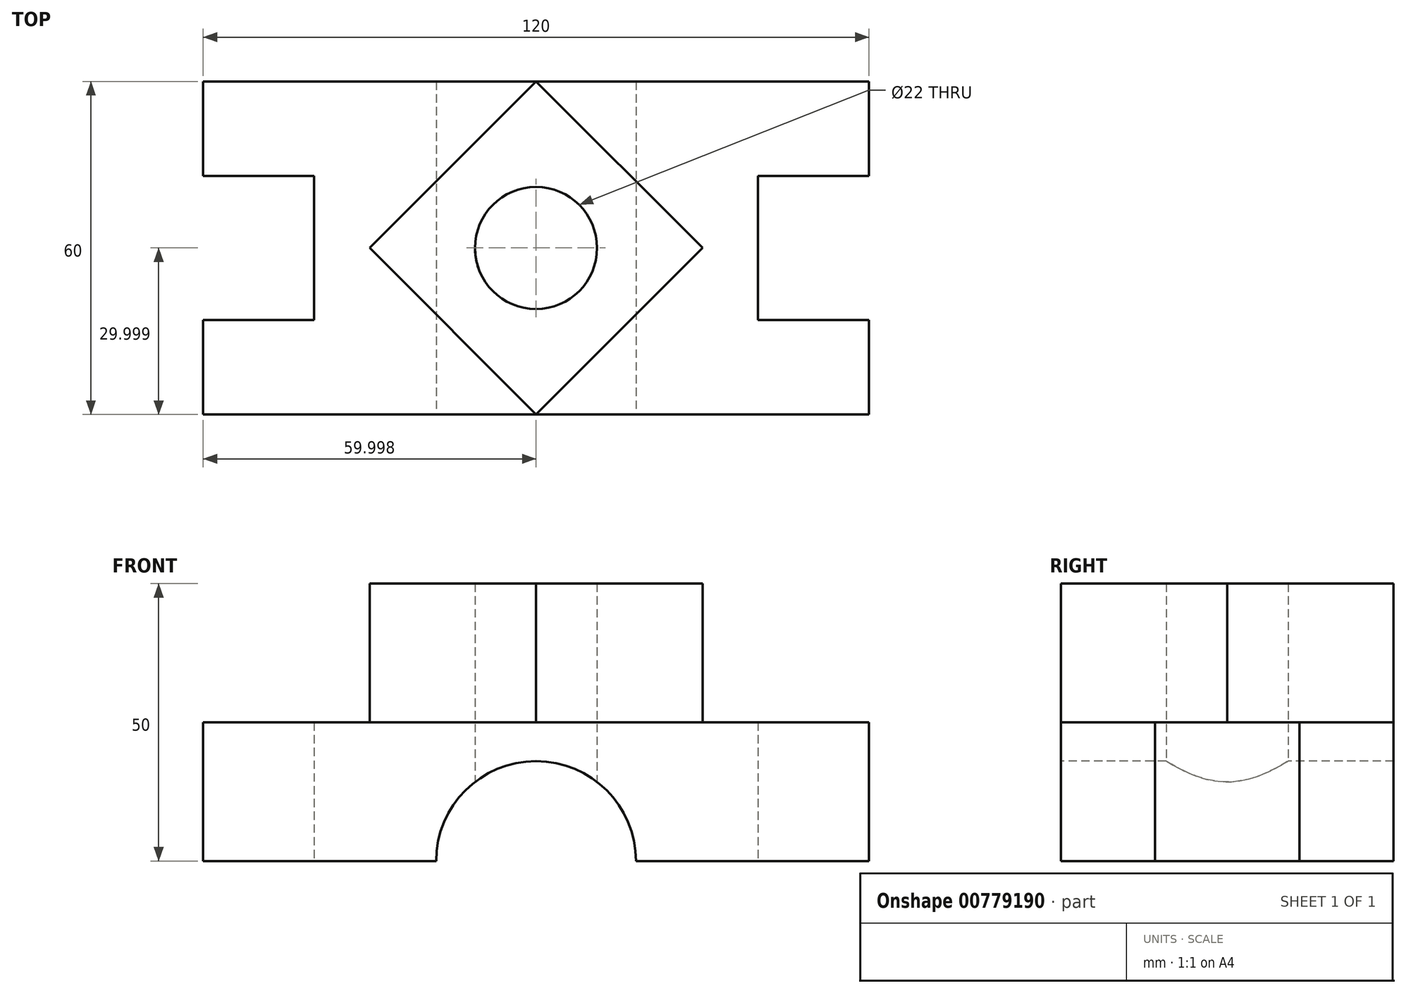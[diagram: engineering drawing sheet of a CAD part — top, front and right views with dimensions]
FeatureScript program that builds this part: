
annotation { "Feature Type Name" : "Feature", "Feature Type Description" : "" }
export const myFeature = defineFeature(function(context is Context, id is Id, definition is map)
    precondition{}
    {
        {
            var Q0;
            Q0=qCreatedBy(makeId("Top.planeOp"),FACE);
            var sketch = newSketch(context, id + "F0", { "sketchPlane" : qUnion([Q0])});
            skLineSegment(sketch, "E0.bottom", {"start": v(-146.92, 73.64) * mm, "end": v(-26.92, 73.64) * mm});
            skLineSegment(sketch, "E0.top", {"start": v(-146.92, 13.64) * mm, "end": v(-26.92, 13.64) * mm});
            skLineSegment(sketch, "E0.left", {"start": v(-146.92, 73.64) * mm, "end": v(-146.92, 56.64) * mm});
            skLineSegment(sketch, "E0.right", {"start": v(-26.92, 73.64) * mm, "end": v(-26.92, 56.64) * mm});
            skLineSegment(sketch, "E1", {"start": v(-146.92, 73.64) * mm, "end": v(-86.92, 73.64) * mm});
            skLineSegment(sketch, "E2", {"start": v(-86.92, 73.64) * mm, "end": v(-86.92, 43.64) * mm});
            skLineSegment(sketch, "E3", {"start": v(-86.92, 43.64) * mm, "end": v(-46.92, 43.64) * mm});
            skLineSegment(sketch, "E4", {"start": v(-26.92, 30.64) * mm, "end": v(-46.92, 30.64) * mm});
            skLineSegment(sketch, "E5", {"start": v(-46.92, 30.64) * mm, "end": v(-46.92, 56.64) * mm});
            skLineSegment(sketch, "E6", {"start": v(-46.92, 56.64) * mm, "end": v(-26.92, 56.64) * mm});
            skLineSegment(sketch, "E7.trimOffspring", {"start": v(-26.92, 30.64) * mm, "end": v(-26.92, 13.64) * mm});
            skPoint(sketch, "E8.orphan", {"position": v(-26.92, 43.64) * mm});
            skLineSegment(sketch, "E9", {"start": v(-86.92, 43.64) * mm, "end": v(-126.92, 43.64) * mm});
            skLineSegment(sketch, "E10", {"start": v(-146.92, 30.64) * mm, "end": v(-126.92, 30.64) * mm});
            skLineSegment(sketch, "E11", {"start": v(-126.92, 30.64) * mm, "end": v(-126.92, 56.64) * mm});
            skLineSegment(sketch, "E12", {"start": v(-126.92, 56.64) * mm, "end": v(-146.92, 56.64) * mm});
            skLineSegment(sketch, "E13.trimOffspring", {"start": v(-146.92, 30.64) * mm, "end": v(-146.92, 13.64) * mm});
            skPoint(sketch, "E14.orphan", {"position": v(-146.92, 43.64) * mm});
            skSolve(sketch);
        }
        {
            var Q0;
            Q0 = qSketchRegion(id + "F0", true);
            extrude(context, id + "F1", {"entities" : qUnion([Q0]), "depth" : 25 * mm, "offsetDistance" : 25 * mm});
        }
        {
            var Q0;
            Q0=makeQuery(id+"F1.opExtrude","CAP_FACE",FACE,{"disambiguationData":[OSD([sQuery(id+"F0.wireOp",EDGE,"E0.bottom"),sQuery(id+"F0.wireOp",EDGE,"E0.top"),sQuery(id+"F0.wireOp",EDGE,"E0.left"),sQuery(id+"F0.wireOp",EDGE,"E0.right"),sQuery(id+"F0.wireOp",EDGE,"E1"),sQuery(id+"F0.wireOp",EDGE,"E4"),sQuery(id+"F0.wireOp",EDGE,"E5"),sQuery(id+"F0.wireOp",EDGE,"E6"),sQuery(id+"F0.wireOp",EDGE,"E7.trimOffspring"),sQuery(id+"F0.wireOp",EDGE,"E10"),sQuery(id+"F0.wireOp",EDGE,"E11"),sQuery(id+"F0.wireOp",EDGE,"E12"),sQuery(id+"F0.wireOp",EDGE,"E13.trimOffspring")])],"isStart":false});
            var sketch = newSketch(context, id + "F2", { "sketchPlane" : qUnion([Q0])});
            skLineSegment(sketch, "E15", {"start": v(-56.92, 43.64) * mm, "end": v(-86.92, 73.64) * mm});
            skLineSegment(sketch, "E16", {"start": v(-116.92, 43.64) * mm, "end": v(-86.92, 73.64) * mm});
            skLineSegment(sketch, "E17", {"start": v(-116.92, 43.64) * mm, "end": v(-86.92, 13.64) * mm});
            skLineSegment(sketch, "E18", {"start": v(-56.92, 43.64) * mm, "end": v(-86.92, 13.64) * mm});
            skCircle(sketch, "E19", {"center": v(-86.92, 43.64) * mm, "radius": 11 * mm});
            skSolve(sketch);
        }
        {
            var Q0;
            Q0 = qSketchRegion(id + "F2", true);
            extrude(context, id + "F3", {"entities" : qUnion([Q0]), "operationType" : NewBodyOperationType.ADD, "depth" : 25 * mm, "offsetDistance" : 25 * mm});
        }
        {
            var Q0;
            Q0=makeQuery(id+"F3.boolean.opBoolean","SPLIT",FACE,{"disambiguationData":[TD([makeQuery(id+"F3.opExtrude","SWEPT_FACE",FACE,{"disambiguationData":[OSD([sQuery(id+"F2.wireOp",EDGE,"E19")])]})])],"derivedFrom":makeQuery(id+"F1.opExtrude","CAP_FACE",FACE,{"disambiguationData":[OSD([sQuery(id+"F0.wireOp",EDGE,"E0.bottom"),sQuery(id+"F0.wireOp",EDGE,"E0.top"),sQuery(id+"F0.wireOp",EDGE,"E0.left"),sQuery(id+"F0.wireOp",EDGE,"E0.right"),sQuery(id+"F0.wireOp",EDGE,"E1"),sQuery(id+"F0.wireOp",EDGE,"E4"),sQuery(id+"F0.wireOp",EDGE,"E5"),sQuery(id+"F0.wireOp",EDGE,"E6"),sQuery(id+"F0.wireOp",EDGE,"E7.trimOffspring"),sQuery(id+"F0.wireOp",EDGE,"E10"),sQuery(id+"F0.wireOp",EDGE,"E11"),sQuery(id+"F0.wireOp",EDGE,"E12"),sQuery(id+"F0.wireOp",EDGE,"E13.trimOffspring")])],"isStart":false})});
            extrude(context, id + "F4", {"entities" : qUnion([Q0]), "operationType" : NewBodyOperationType.REMOVE, "oppositeDirection" : true, "depth" : 50 * mm, "offsetDistance" : 25 * mm});
        }
        {
            var Q0;
            Q0=makeQuery(id+"F1.opExtrude","SWEPT_FACE",FACE,{"disambiguationData":[OSD([sQuery(id+"F0.wireOp",EDGE,"E0.top")])]});
            var sketch = newSketch(context, id + "F5", { "sketchPlane" : qUnion([Q0])});
            skLineSegment(sketch, "E20", {"start": v(-68.92, 0) * mm, "end": v(-26.92, 0) * mm});
            skLineSegment(sketch, "E21", {"start": v(-104.92, 0) * mm, "end": v(-86.92, 0) * mm});
            skArc(sketch, "E22", {"start": v(-68.92, 0) * mm, "mid": v(-86.92, 18) * mm, "end": v(-104.92, 0) * mm});
            skLineSegment(sketch, "E23", {"start": v(-104.92, 0) * mm, "end": v(-68.92, 0) * mm});
            skSolve(sketch);
        }
        {
            var Q0;
            {var subQ0=sQuery(id+"F5.wireOp",EDGE,"E22");Q0=makeQuery(id+"F5.imprint","IMPRINT",FACE,{"disambiguationData":[TD([[makeQuery(id+"F5.imprint","IMPRINT",EDGE,{"derivedFrom":subQ0}),1.0]])]});}
            extrude(context, id + "F6", {"entities" : qUnion([Q0]), "operationType" : NewBodyOperationType.REMOVE, "oppositeDirection" : true, "depth" : 60 * mm, "offsetDistance" : 25 * mm});
        }
    });
